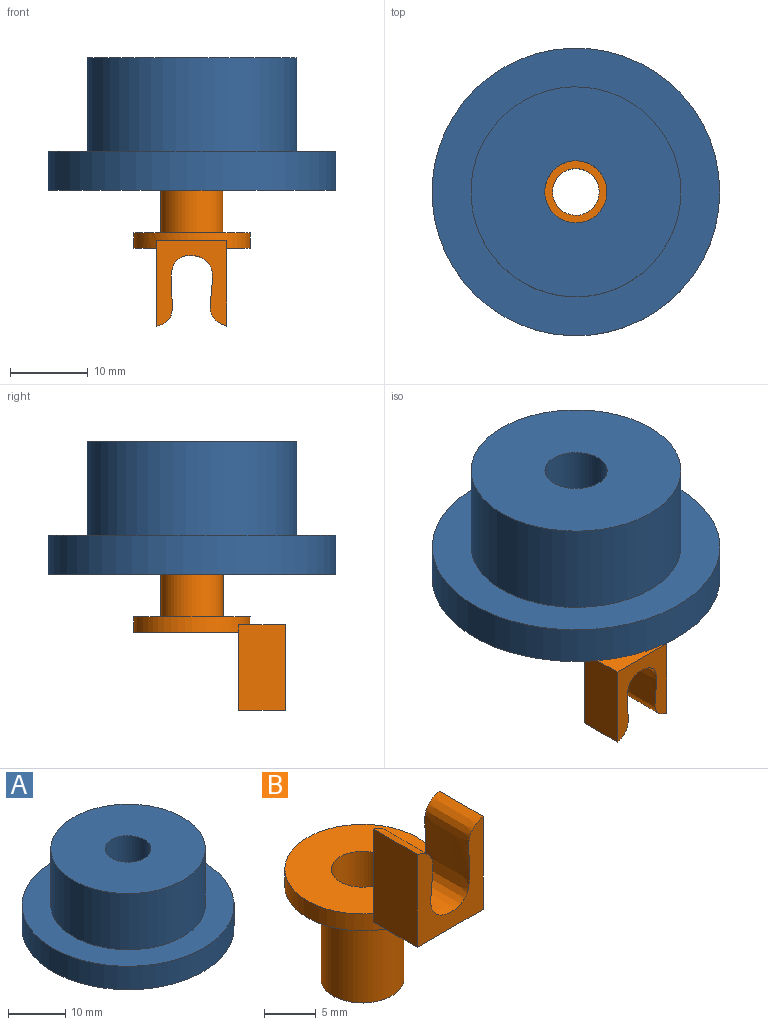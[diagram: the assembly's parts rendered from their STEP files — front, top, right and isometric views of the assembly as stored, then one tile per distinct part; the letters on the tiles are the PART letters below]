
ASSEMBLY  parts=2 mates=1
PART A: 6 faces, bbox 37x37x17 mm
  f0: cylinder r=13.5mm len=27mm, axis (0,0,-1), area 1017.9mm2, adj f2,f5
  f1: cylinder r=4mm len=17mm, axis (0,0,-1), area 427.3mm2, adj f2,f3
  f2: plane 27x27mm, normal (0,0,1), area 522.3mm2, adj f0,f1
  f3: plane 37x37mm, normal (0,0,-1), area 1024.9mm2, adj f1,f4
  f4: cylinder r=18.5mm len=37mm, axis (0,0,-1), area 581.2mm2, adj f3,f5
  f5: plane 37x37mm, normal (0,0,1), area 502.7mm2, adj f0,f4
PART B: 12 faces, bbox 15x19.5x23 mm
  f0: cylinder r=7.5mm len=15mm, axis (0,0,1), area 84.6mm2, adj f1,f2,f6,f7,f8
  f1: plane 15x13.5mm, normal (0,0,1), area 139.2mm2, adj f0,f4,f11
  f2: plane 15x15mm, normal (0,0,-1), area 126.4mm2, adj f0,f3
  f3: cylinder r=4mm len=11mm, axis (0,0,1), area 276.5mm2, adj f2,f5
  f4: cylinder r=3mm len=13mm, axis (0,0,1), area 245mm2, adj f1,f5
  f5: plane 8x8mm, normal (0,0,-1), area 22mm2, adj f3,f4
  f6: plane 11x6mm, normal (-1,0,0), area 66mm2, adj f0,f7,f9,f10,f11
  f7: plane 9x6mm, normal (0,0,-1), area 44.8mm2, adj f0,f6,f8,f10
  f8: plane 11x6mm, normal (1,0,0), area 66mm2, adj f0,f7,f9,f10,f11
  f9: extruded ~9.09x9mm, area 141mm2, adj f6,f8,f10,f11
  f10: plane 11x9mm, normal (0,-1,0), area 52.8mm2, adj f6,f7,f8,f9
  f11: plane 10x9mm, normal (0,1,0), area 43.8mm2, adj f1,f6,f8,f9
PLACE A t=(-1.16,-0.68,2.04)mm
PLACE B rot(axis=(0,-1,0),180deg) t=(3.34,-6.68,-5.46)mm
MATE revolute B.f0 <-> A.f1  axis (0,0,-1) through (-1.16,-0.68,2.04)mm
